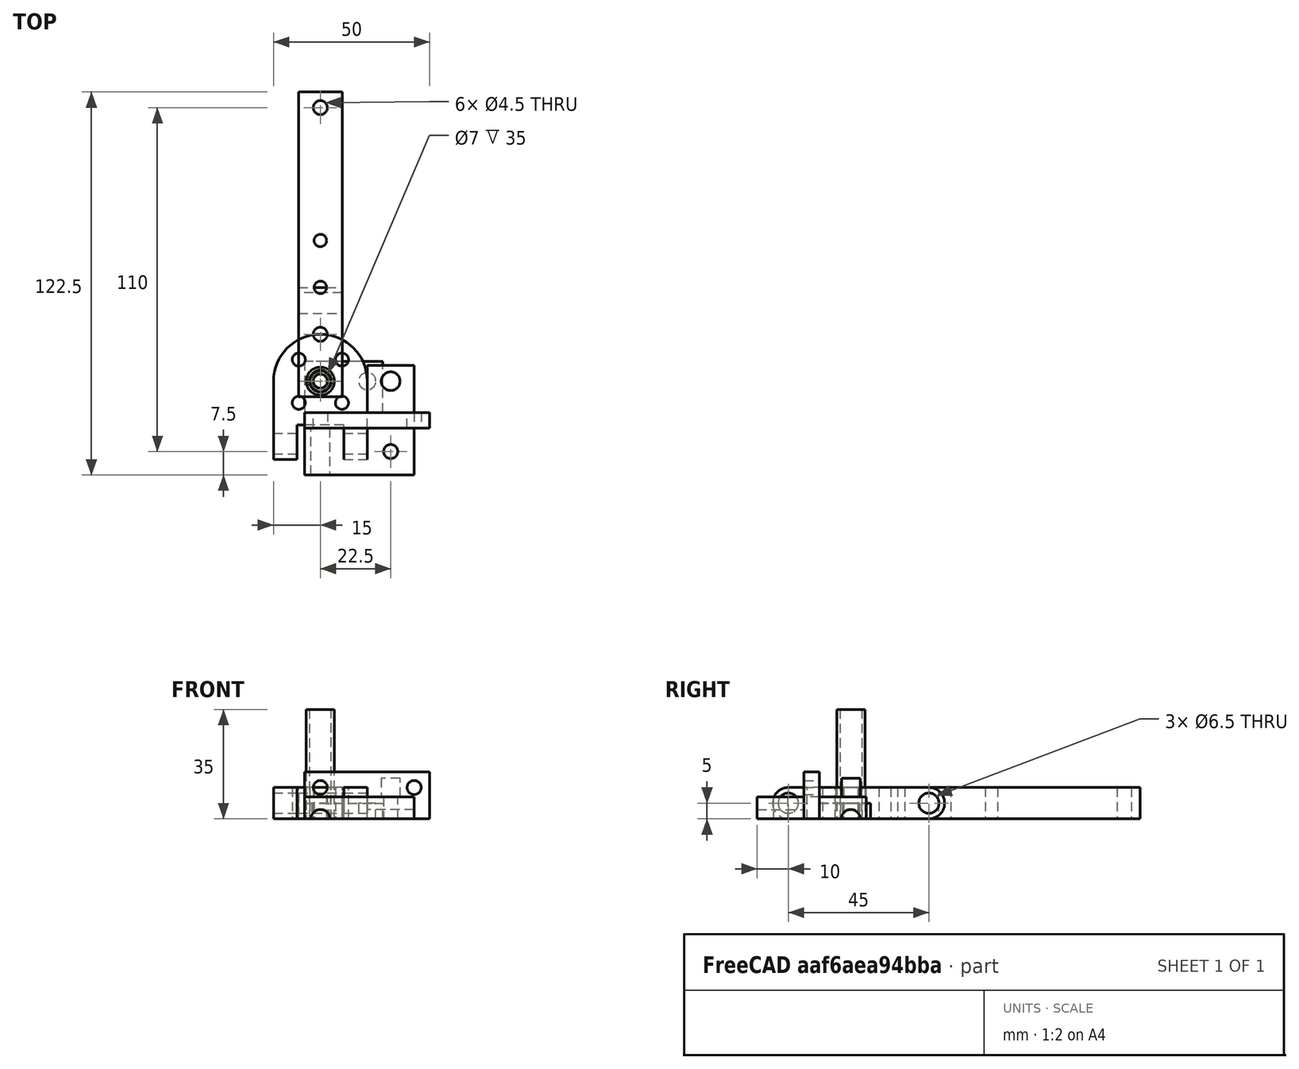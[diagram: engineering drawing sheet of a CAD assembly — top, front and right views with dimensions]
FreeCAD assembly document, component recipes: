
FREECAD ASSEMBLY — COMPONENT RECIPES ("A4_PAINT_ROLLER_1V0")

This assembly document has 6 components, labeled P0..P5 below (a component is one placed body or linked part). 6 of them carry a construction recipe — the FreeCAD feature program that regenerates the part from scratch, quoted from this document or its linked companion documents; the rest are supplied as boundary geometry only. No exploded tour is included for this assembly.
COMPONENT P0 — recipe-attached ("LOAD_CELL_BRACKET_1_0", modeled in this document).
Construction recipe (the document's own serialized feature program — sketch geometry with constraints, then the solid features built on it; lengths are millimeters unless a unit is written):

FEATURE [PartDesign::CoordinateSystem] LCS_0001
  AttacherType = Attacher::AttachEngine3D
  MapMode = 2
  Support = -> [X_Axis002]
FEATURE [Sketcher::SketchObject] Sketch
  FullyConstrained = true
  MapMode = 5
  Support = -> [XY_Plane002]
  sketch-geometry (6):
    g0: Circle CenterX=0 CenterY=0 CenterZ=0 NormalX=0 NormalY=0 NormalZ=1 AngleXU=0 Radius=2.75
    g1: Circle CenterX=15 CenterY=0 CenterZ=0 NormalX=0 NormalY=0 NormalZ=1 AngleXU=0 Radius=2.75
    g2: LineSegment StartX=-5 StartY=-15 StartZ=0 EndX=20 EndY=-15 EndZ=0
    g3: LineSegment StartX=20 StartY=-15 StartZ=0 EndX=20 EndY=6.35 EndZ=0
    g4: LineSegment StartX=20 StartY=6.35 StartZ=0 EndX=-5 EndY=6.35 EndZ=0
    g5: LineSegment StartX=-5 StartY=6.35 StartZ=0 EndX=-5 EndY=-15 EndZ=0
  constraints (17):
    c: Coincident(g0,g-1)
    c: PointOnObject(g1,g-1)
    c: Diameter(g0) = 5.5
    c: Equal(g0,g1)
    c: DistanceX(g0,g1) = 15
    c: Coincident(g2,g3)
    c: Coincident(g3,g4)
    c: Coincident(g4,g5)
    c: Coincident(g5,g2)
    c: Horizontal(g2)
    c: Horizontal(g4)
    c: Vertical(g3)
    c: Vertical(g5)
    c: DistanceY(g-1,g4) = 6.35
    c: DistanceX(g4,g-1) = 5
    c: DistanceX(g1,g3) = 5
    c: DistanceY(g2,g-1) = 15
FEATURE [PartDesign::Pad] Pad
  Direction = (1,1,1)
  Length = 5
  Length2 = 100
  Profile = -> Sketch
  Refine = true
  Type = 0
FEATURE [Sketcher::SketchObject] Sketch013
  AttachmentOffset = pos=(0,0,10) rot=(0,0,1;0rad)
  FullyConstrained = true
  MapMode = 5
  Placement = pos=(0,-10,-2.2e-15) rot=(1,0,0;1.5708rad)
  Support = -> [XZ_Plane002]
  sketch-geometry (6):
    g0: LineSegment StartX=-5 StartY=0 StartZ=0 EndX=35 EndY=0 EndZ=0
    g1: LineSegment StartX=35 StartY=0 StartZ=0 EndX=35 EndY=15 EndZ=0
    g2: LineSegment StartX=35 StartY=15 StartZ=0 EndX=-5 EndY=15 EndZ=0
    g3: LineSegment StartX=-5 StartY=15 StartZ=0 EndX=-5 EndY=0 EndZ=0
    g4: Circle CenterX=0 CenterY=10 CenterZ=0 NormalX=0 NormalY=0 NormalZ=1 AngleXU=0 Radius=2.25
    g5: Circle CenterX=30 CenterY=10 CenterZ=0 NormalX=0 NormalY=0 NormalZ=1 AngleXU=0 Radius=2.25
  constraints (18):
    c: Coincident(g0,g1)
    c: Coincident(g1,g2)
    c: Coincident(g2,g3)
    c: Coincident(g3,g0)
    c: Horizontal(g0)
    c: Horizontal(g2)
    c: Vertical(g1)
    c: Vertical(g3)
    c: PointOnObject(g0,g-1)
    c: DistanceX(g2,g-1) = 5
    c: PointOnObject(g4,g-2)
    c: Diameter(g5) = 4.5
    c: Equal(g5,g4)
    c: DistanceX(g4,g5) = 30
    c: DistanceX(g5,g1) = 5
    c: DistanceY(g-1,g4) = 10
    c: Horizontal(g4,g5)
    c: DistanceY(g4,g2) = 5
FEATURE [PartDesign::Pad] Pad008
  BaseFeature = -> Pad
  Direction = (1,1,1)
  Length = 5
  Length2 = 100
  Profile = -> Sketch013
  Refine = true
  Type = 0
FEATURE [PartDesign::Body] Body
  Group = -> [LCS_0001,Sketch,Pad,Sketch013,Pad008]
  Origin = -> Origin002
  Tip = -> Pad008
COMPONENT P1 — recipe-attached ("ROLLER_BRACKET_1_0", modeled in this document).
Construction recipe (the document's own serialized feature program — sketch geometry with constraints, then the solid features built on it; lengths are millimeters unless a unit is written):

FEATURE [PartDesign::CoordinateSystem] LCS_0003
  AttacherType = Attacher::AttachEngine3D
  MapMode = 2
  Support = -> [X_Axis004]
FEATURE [Sketcher::SketchObject] Sketch002
  FullyConstrained = true
  MapMode = 5
  Support = -> [XY_Plane004]
  expr: Constraints[1] = Variables.hubHolePD
  sketch-geometry (14):
    g0: Circle CenterX=0 CenterY=0 CenterZ=0 NormalX=0 NormalY=0 NormalZ=1 AngleXU=0 Radius=9.779
    g1: LineSegment StartX=-6.9148 StartY=6.9148 StartZ=0 EndX=6.9148 EndY=6.9148 EndZ=0
    g2: LineSegment StartX=6.9148 StartY=6.9148 StartZ=0 EndX=6.9148 EndY=-6.9148 EndZ=0
    g3: LineSegment StartX=6.9148 StartY=-6.9148 StartZ=0 EndX=-6.9148 EndY=-6.9148 EndZ=0
    g4: LineSegment StartX=-6.9148 StartY=-6.9148 StartZ=0 EndX=-6.9148 EndY=6.9148 EndZ=0
    g5: Circle CenterX=0 CenterY=0 CenterZ=0 NormalX=0 NormalY=0 NormalZ=1 AngleXU=0 Radius=3.35
    g6: Circle CenterX=-6.9148 CenterY=6.9148 CenterZ=0 NormalX=0 NormalY=0 NormalZ=1 AngleXU=0 Radius=2.1
    g7: Circle CenterX=6.9148 CenterY=6.9148 CenterZ=0 NormalX=0 NormalY=0 NormalZ=1 AngleXU=0 Radius=2.1
    g8: Circle CenterX=6.9148 CenterY=-6.9148 CenterZ=0 NormalX=0 NormalY=0 NormalZ=1 AngleXU=0 Radius=2.1
    g9: Circle CenterX=-6.9148 CenterY=-6.9148 CenterZ=0 NormalX=0 NormalY=0 NormalZ=1 AngleXU=0 Radius=2.1
    g10: ArcOfCircle CenterX=0 CenterY=0 CenterZ=0 NormalX=0 NormalY=0 NormalZ=1 AngleXU=0 Radius=15 StartAngle=0 EndAngle=3.14159
    g11: LineSegment StartX=-15 StartY=1.8e-15 StartZ=0 EndX=-15 EndY=-25 EndZ=0
    g12: LineSegment StartX=-15 StartY=-25 StartZ=0 EndX=15 EndY=-25 EndZ=0
    g13: LineSegment StartX=15 StartY=-25 StartZ=0 EndX=15 EndY=0 EndZ=0
  constraints (35):
    c: Coincident(g0,g-1)
    c: Diameter(g0) = 19.558
    c: Coincident(g1,g2)
    c: Coincident(g2,g3)
    c: Coincident(g3,g4)
    c: Coincident(g4,g1)
    c: Horizontal(g1)
    c: Horizontal(g3)
    c: Vertical(g2)
    c: Vertical(g4)
    c: PointOnObject(g1,g0)
    c: PointOnObject(g2,g0)
    c: PointOnObject(g1,g0)
    c: Equal(g1,g4)
    c: Coincident(g5,g-1)
    c: Diameter(g5) = 6.7
    c: Coincident(g6,g1)
    c: Coincident(g7,g1)
    c: Coincident(g8,g2)
    c: Coincident(g9,g3)
    c: Diameter(g9) = 4.2
    c: Equal(g9,g8)
    c: Equal(g9,g7)
    c: Equal(g9,g6)
    c: Coincident(g10,g5)
    c: PointOnObject(g10,g-1)
    c: PointOnObject(g10,g-1)
    c: Diameter(g10) = 30
    c: Tangent(g10,g11) = -1.5708
    c: Coincident(g11,g12)
    c: Horizontal(g12)
    c: Coincident(g12,g13)
    c: Coincident(g13,g10)
    c: Vertical(g13)
    c: DistanceY(g11,g11) = 25
FEATURE [PartDesign::Pad] Pad002
  Direction = (1,1,1)
  Length = 10
  Length2 = 100
  Profile = -> Sketch002
  Refine = true
  Type = 0
FEATURE [Sketcher::SketchObject] Sketch003
  FullyConstrained = true
  MapMode = 5
  Placement = pos=(0,0,0) rot=(0.57735,0.57735,0.57735;2.0944rad)
  Support = -> [YZ_Plane004]
  sketch-geometry (5):
    g0: Circle CenterX=-20 CenterY=5 CenterZ=0 NormalX=0 NormalY=0 NormalZ=1 AngleXU=0 Radius=3.25
    g1: ArcOfCircle CenterX=-20 CenterY=5 CenterZ=0 NormalX=0 NormalY=0 NormalZ=1 AngleXU=0 Radius=5 StartAngle=1.5708 EndAngle=4.71239
    g2: LineSegment StartX=-20 StartY=10 StartZ=0 EndX=-26 EndY=10 EndZ=0
    g3: LineSegment StartX=-26 StartY=10 StartZ=0 EndX=-26 EndY=0 EndZ=0
    g4: LineSegment StartX=-26 StartY=0 StartZ=0 EndX=-20 EndY=2.62519e-11 EndZ=0
  constraints (15):
    c: Diameter(g0) = 6.5
    c: DistanceY(g-1,g0) = 5
    c: Coincident(g1,g0)
    c: PointOnObject(g1,g-1)
    c: Diameter(g1) = 10
    c: Coincident(g1,g2)
    c: Coincident(g2,g3)
    c: PointOnObject(g3,g-1)
    c: Coincident(g3,g4)
    c: Coincident(g4,g1)
    c: Vertical(g3)
    c: Vertical(g0,g1)
    c: Horizontal(g2)
    c: DistanceX(g0,g-1) = 20
    c: DistanceX(g2,g2) = 6
FEATURE [PartDesign::Pocket] Pocket
  BaseFeature = -> Pad002
  Length = 5
  Length2 = 100
  Midplane = true
  Profile = -> Sketch003
  Refine = true
  Type = 1
FEATURE [Sketcher::SketchObject] Sketch004
  FullyConstrained = true
  MapMode = 5
  Placement = pos=(0,0,0) rot=(0.57735,0.57735,0.57735;2.0944rad)
  Support = -> [YZ_Plane004]
  sketch-geometry (4):
    g0: LineSegment StartX=-25 StartY=0 StartZ=0 EndX=-14 EndY=0 EndZ=0
    g1: LineSegment StartX=-14 StartY=0 StartZ=0 EndX=-14 EndY=11 EndZ=0
    g2: LineSegment StartX=-14 StartY=11 StartZ=0 EndX=-25 EndY=11 EndZ=0
    g3: LineSegment StartX=-25 StartY=11 StartZ=0 EndX=-25 EndY=0 EndZ=0
  constraints (12):
    c: Coincident(g0,g1)
    c: Coincident(g1,g2)
    c: Coincident(g2,g3)
    c: Coincident(g3,g0)
    c: Horizontal(g0)
    c: Horizontal(g2)
    c: Vertical(g1)
    c: Vertical(g3)
    c: PointOnObject(g0,g-1)
    c: DistanceX(g2,g2) = 11
    c: DistanceX(g1,g-1) = 14
    c: Equal(g3,g2)
FEATURE [PartDesign::Pocket] Pocket001
  BaseFeature = -> Pocket
  Length = 15
  Length2 = 100
  Midplane = true
  Profile = -> Sketch004
  Refine = true
  Type = 0
FEATURE [PartDesign::Body] Body_2
  Group = -> [LCS_0003,Sketch002,Pad002,Sketch003,Pocket,Sketch004,Pocket001]
  Origin = -> Origin004
  Tip = -> Pocket001
COMPONENT P2 — recipe-attached ("ROLLER_BRACKET_B_1_0", modeled in this document).
Construction recipe (the document's own serialized feature program — sketch geometry with constraints, then the solid features built on it; lengths are millimeters unless a unit is written):

FEATURE [PartDesign::CoordinateSystem] LCS_0005
  AttacherType = Attacher::AttachEngine3D
  MapMode = 2
  Support = -> [X_Axis006]
FEATURE [Sketcher::SketchObject] Sketch005
  FullyConstrained = true
  MapMode = 5
  Support = -> [XY_Plane006]
  sketch-geometry (6):
    g0: LineSegment StartX=-7 StartY=-5 StartZ=0 EndX=7 EndY=-5 EndZ=0
    g1: LineSegment StartX=7 StartY=-5 StartZ=0 EndX=7 EndY=30 EndZ=0
    g2: LineSegment StartX=7 StartY=30 StartZ=0 EndX=-7 EndY=30 EndZ=0
    g3: LineSegment StartX=-7 StartY=30 StartZ=0 EndX=-7 EndY=-5 EndZ=0
    g4: Circle CenterX=0 CenterY=0 CenterZ=0 NormalX=0 NormalY=0 NormalZ=1 AngleXU=0 Radius=2.25
    g5: Circle CenterX=0 CenterY=15 CenterZ=0 NormalX=0 NormalY=0 NormalZ=1 AngleXU=0 Radius=2.25
  constraints (16):
    c: Coincident(g0,g1)
    c: Coincident(g1,g2)
    c: Coincident(g2,g3)
    c: Coincident(g3,g0)
    c: Horizontal(g2)
    c: Vertical(g1)
    c: Vertical(g3)
    c: Coincident(g4,g-1)
    c: PointOnObject(g5,g-2)
    c: Diameter(g5) = 4.5
    c: Equal(g5,g4)
    c: Symmetric(g0,g0,g-2)
    c: DistanceX(g0,g0) = 14
    c: DistanceY(g0,g-1) = 5
    c: DistanceY(g5,g1) = 15
    c: DistanceY(g4,g5) = 15
FEATURE [PartDesign::Pad] Pad003
  Direction = (1,1,1)
  Length = 10
  Length2 = 100
  Profile = -> Sketch005
  Refine = true
  Type = 0
FEATURE [Sketcher::SketchObject] Sketch006
  FullyConstrained = true
  MapMode = 5
  Placement = pos=(0,0,0) rot=(0.57735,0.57735,0.57735;2.0944rad)
  Support = -> [YZ_Plane006]
  sketch-geometry (5):
    g0: Circle CenterX=25 CenterY=5 CenterZ=0 NormalX=0 NormalY=0 NormalZ=1 AngleXU=0 Radius=3.25
    g1: ArcOfCircle CenterX=25 CenterY=5 CenterZ=0 NormalX=0 NormalY=0 NormalZ=1 AngleXU=0 Radius=5 StartAngle=4.71239 EndAngle=7.85398
    g2: LineSegment StartX=25 StartY=10 StartZ=0 EndX=31 EndY=10 EndZ=0
    g3: LineSegment StartX=31 StartY=10 StartZ=0 EndX=31 EndY=0 EndZ=0
    g4: LineSegment StartX=31 StartY=0 StartZ=0 EndX=25 EndY=0 EndZ=0
  constraints (15):
    c: Diameter(g0) = 6.5
    c: Coincident(g1,g0)
    c: PointOnObject(g1,g-1)
    c: Vertical(g1,g0)
    c: Vertical(g0,g1)
    c: Diameter(g1) = 10
    c: Coincident(g1,g2)
    c: Coincident(g2,g3)
    c: PointOnObject(g3,g-1)
    c: Coincident(g3,g4)
    c: Coincident(g4,g1)
    c: Vertical(g3)
    c: Horizontal(g2)
    c: DistanceX(g-1,g0) = 25
    c: DistanceX(g2,g2) = 6
FEATURE [PartDesign::Pocket] Pocket002
  BaseFeature = -> Pad003
  Length = 5
  Length2 = 100
  Midplane = true
  Profile = -> Sketch006
  Refine = true
  Type = 1
FEATURE [PartDesign::Body] Body_3
  Group = -> [LCS_0005,Sketch005,Pad003,Sketch006,Pocket002]
  Origin = -> Origin006
  Tip = -> Pocket002
COMPONENT P3 — recipe-attached ("SPRING-1.0", modeled in this document).
Construction recipe (the document's own serialized feature program — sketch geometry with constraints, then the solid features built on it; lengths are millimeters unless a unit is written):

FEATURE [PartDesign::CoordinateSystem] LCS_0011
  AttacherType = Attacher::AttachEngine3D
  MapMode = 2
  Support = -> [X_Axis012]
FEATURE [Sketcher::SketchObject] Sketch012
  FullyConstrained = true
  MapMode = 5
  Support = -> [XY_Plane012]
  sketch-geometry (2):
    g0: Circle CenterX=0 CenterY=0 CenterZ=0 NormalX=0 NormalY=0 NormalZ=1 AngleXU=0 Radius=4.5
    g1: Circle CenterX=0 CenterY=0 CenterZ=0 NormalX=0 NormalY=0 NormalZ=1 AngleXU=0 Radius=3.5
  constraints (4):
    c: Coincident(g0,g-1)
    c: Coincident(g1,g0)
    c: Diameter(g1) = 7
    c: Diameter(g0) = 9
FEATURE [PartDesign::Pad] Pad007
  Direction = (1,1,1)
  Length = 35
  Length2 = 100
  Profile = -> Sketch012
  Refine = true
  Type = 0
FEATURE [PartDesign::Body] Body_6
  Group = -> [LCS_0011,Sketch012,Pad007]
  Origin = -> Origin012
  Tip = -> Pad007
COMPONENT P4 — recipe-attached ("SPRING_BRACKET_1_0", modeled in this document).
Construction recipe (the document's own serialized feature program — sketch geometry with constraints, then the solid features built on it; lengths are millimeters unless a unit is written):

FEATURE [PartDesign::CoordinateSystem] LCS_0007
  AttacherType = Attacher::AttachEngine3D
  MapMode = 2
  Support = -> [X_Axis008]
FEATURE [Sketcher::SketchObject] Sketch007
  FullyConstrained = true
  MapMode = 5
  Support = -> [XY_Plane008]
  expr: Constraints[17] = Variables.springBracketL
  sketch-geometry (9):
    g0: LineSegment StartX=-7 StartY=-5 StartZ=0 EndX=7 EndY=-5 EndZ=0
    g1: LineSegment StartX=7 StartY=-5 StartZ=0 EndX=7 EndY=92.5 EndZ=0
    g2: LineSegment StartX=7 StartY=92.5 StartZ=0 EndX=-7 EndY=92.5 EndZ=0
    g3: LineSegment StartX=-7 StartY=92.5 StartZ=0 EndX=-7 EndY=-5 EndZ=0
    g4: Circle CenterX=0 CenterY=0 CenterZ=0 NormalX=0 NormalY=0 NormalZ=1 AngleXU=0 Radius=2.25
    g5: Circle CenterX=0 CenterY=15 CenterZ=0 NormalX=0 NormalY=0 NormalZ=1 AngleXU=0 Radius=2.25
    g6: Circle CenterX=0 CenterY=87.5 CenterZ=0 NormalX=0 NormalY=0 NormalZ=1 AngleXU=0 Radius=2.25
    g7: Circle CenterX=0 CenterY=30 CenterZ=0 NormalX=0 NormalY=0 NormalZ=1 AngleXU=0 Radius=2
    g8: Circle CenterX=0 CenterY=45 CenterZ=0 NormalX=0 NormalY=0 NormalZ=1 AngleXU=0 Radius=2
  constraints (25):
    c: Coincident(g0,g1)
    c: Coincident(g1,g2)
    c: Coincident(g2,g3)
    c: Coincident(g3,g0)
    c: Horizontal(g2)
    c: Vertical(g1)
    c: Vertical(g3)
    c: Coincident(g4,g-1)
    c: Symmetric(g0,g0,g-2)
    c: DistanceX(g0,g0) = 14
    c: Diameter(g4) = 4.5
    c: PointOnObject(g5,g-2)
    c: Equal(g5,g4)
    c: DistanceY(g4,g5) = 15
    c: DistanceY(g0,g4) = 5
    c: PointOnObject(g6,g-2)
    c: Diameter(g6) = 4.5
    c: DistanceY(g-1,g6) = 87.5
    c: DistanceY(g6,g1) = 5
    c: PointOnObject(g7,g-2)
    c: PointOnObject(g8,g-2)
    c: Diameter(g8) = 4
    c: Equal(g8,g7)
    c: DistanceY(g7,g8) = 15
    c: DistanceY(g5,g7) = 15
FEATURE [PartDesign::Pad] Pad004
  Direction = (1,1,1)
  Length = 10
  Length2 = 100
  Profile = -> Sketch007
  Refine = true
  Type = 0
FEATURE [PartDesign::Body] Body_4
  Group = -> [LCS_0007,Sketch007,Pad004]
  Origin = -> Origin008
  Tip = -> Pad004
COMPONENT P5 — recipe-attached ("SPRING_CLAMP_1_0", modeled in this document).
Construction recipe (the document's own serialized feature program — sketch geometry with constraints, then the solid features built on it; lengths are millimeters unless a unit is written):

FEATURE [PartDesign::CoordinateSystem] LCS_0009
  AttacherType = Attacher::AttachEngine3D
  MapMode = 2
  Support = -> [X_Axis010]
FEATURE [Sketcher::SketchObject] Sketch008
  FullyConstrained = true
  MapMode = 5
  Support = -> [XY_Plane010]
  sketch-geometry (7):
    g0: LineSegment StartX=-5 StartY=-30 StartZ=0 EndX=-5 EndY=-15 EndZ=0
    g1: LineSegment StartX=-5 StartY=-15 StartZ=0 EndX=15 EndY=-15 EndZ=0
    g2: LineSegment StartX=15 StartY=-15 StartZ=0 EndX=15 EndY=5 EndZ=0
    g3: LineSegment StartX=15 StartY=5 StartZ=0 EndX=30 EndY=5 EndZ=0
    g4: LineSegment StartX=30 StartY=5 StartZ=0 EndX=30 EndY=-30 EndZ=0
    g5: LineSegment StartX=30 StartY=-30 StartZ=0 EndX=-5 EndY=-30 EndZ=0
    g6: Circle CenterX=22.5 CenterY=-22.5 CenterZ=0 NormalX=0 NormalY=0 NormalZ=1 AngleXU=0 Radius=2.25
  constraints (21):
    c: Vertical(g0)
    c: Coincident(g0,g1)
    c: Horizontal(g1)
    c: Coincident(g1,g2)
    c: Vertical(g2)
    c: Coincident(g2,g3)
    c: Horizontal(g3)
    c: Coincident(g3,g4)
    c: Vertical(g4)
    c: Coincident(g4,g5)
    c: Coincident(g5,g0)
    c: Horizontal(g5)
    c: DistanceX(g-1,g2) = 15
    c: DistanceY(g0,g-1) = 15
    c: DistanceY(g0,g0) = 15
    c: Equal(g0,g3)
    c: Diameter(g6) = 4.5
    c: DistanceY(g6,g1) = 7.5
    c: DistanceX(g1,g6) = 7.5
    c: DistanceY(g-1,g3) = 5
    c: DistanceX(g0,g-1) = 5
FEATURE [PartDesign::Pad] Pad005
  Direction = (1,1,1)
  Length = 7
  Length2 = 100
  Profile = -> Sketch008
  Refine = true
  Type = 0
FEATURE [Sketcher::SketchObject] Sketch009
  FullyConstrained = true
  MapMode = 5
  Placement = pos=(0,0,0) rot=(1,0,0;1.5708rad)
  Support = -> [XZ_Plane010]
  sketch-geometry (1):
    g0: Circle CenterX=0 CenterY=0 CenterZ=0 NormalX=0 NormalY=0 NormalZ=1 AngleXU=0 Radius=3
  constraints (2):
    c: Coincident(g0,g-1)
    c: Diameter(g0) = 6
FEATURE [PartDesign::Pocket] Pocket003
  BaseFeature = -> Pad005
  Length = 5
  Length2 = 100
  Profile = -> Sketch009
  Refine = true
  Reversed = true
  Type = 1
FEATURE [Sketcher::SketchObject] Sketch010
  FullyConstrained = true
  MapMode = 5
  Placement = pos=(0,0,0) rot=(0.57735,0.57735,0.57735;2.0944rad)
  Support = -> [YZ_Plane010]
  sketch-geometry (1):
    g0: Circle CenterX=0 CenterY=0 CenterZ=0 NormalX=0 NormalY=0 NormalZ=1 AngleXU=0 Radius=3
  constraints (2):
    c: Coincident(g0,g-1)
    c: Diameter(g0) = 6
FEATURE [PartDesign::Pocket] Pocket004
  BaseFeature = -> Pocket003
  Length = 5
  Length2 = 100
  Profile = -> Sketch010
  Refine = true
  Reversed = true
  Type = 1
FEATURE [Sketcher::SketchObject] Sketch011
  AttachmentOffset = pos=(0,0,7) rot=(0,0,1;0rad)
  FullyConstrained = true
  MapMode = 5
  Placement = pos=(0,0,7) rot=(0,0,1;0rad)
  Support = -> [XY_Plane010]
  sketch-geometry (1):
    g0: Circle CenterX=22.5 CenterY=0 CenterZ=0 NormalX=0 NormalY=0 NormalZ=1 AngleXU=0 Radius=3
  constraints (3):
    c: PointOnObject(g0,g-1)
    c: Diameter(g0) = 6
    c: DistanceX(g-1,g0) = 22.5
FEATURE [PartDesign::Pad] Pad006
  BaseFeature = -> Pocket004
  Direction = (1,1,1)
  Length = 6
  Length2 = 100
  Profile = -> Sketch011
  Refine = true
  Type = 0
FEATURE [PartDesign::Body] Body_5
  Group = -> [LCS_0009,Sketch008,Pad005,Sketch009,Pocket003,Sketch010,Pocket004,Sketch011,Pad006]
  Origin = -> Origin010
  Tip = -> Pad006
PROVENANCE & LICENSES
A FreeCAD (.FCStd) document from a public repository crawl; recipes are the document's own serialized feature recipes (and, for linked parts, companion documents' recipes).
License: as declared in the source repository (recorded in the dataset sidecar).
